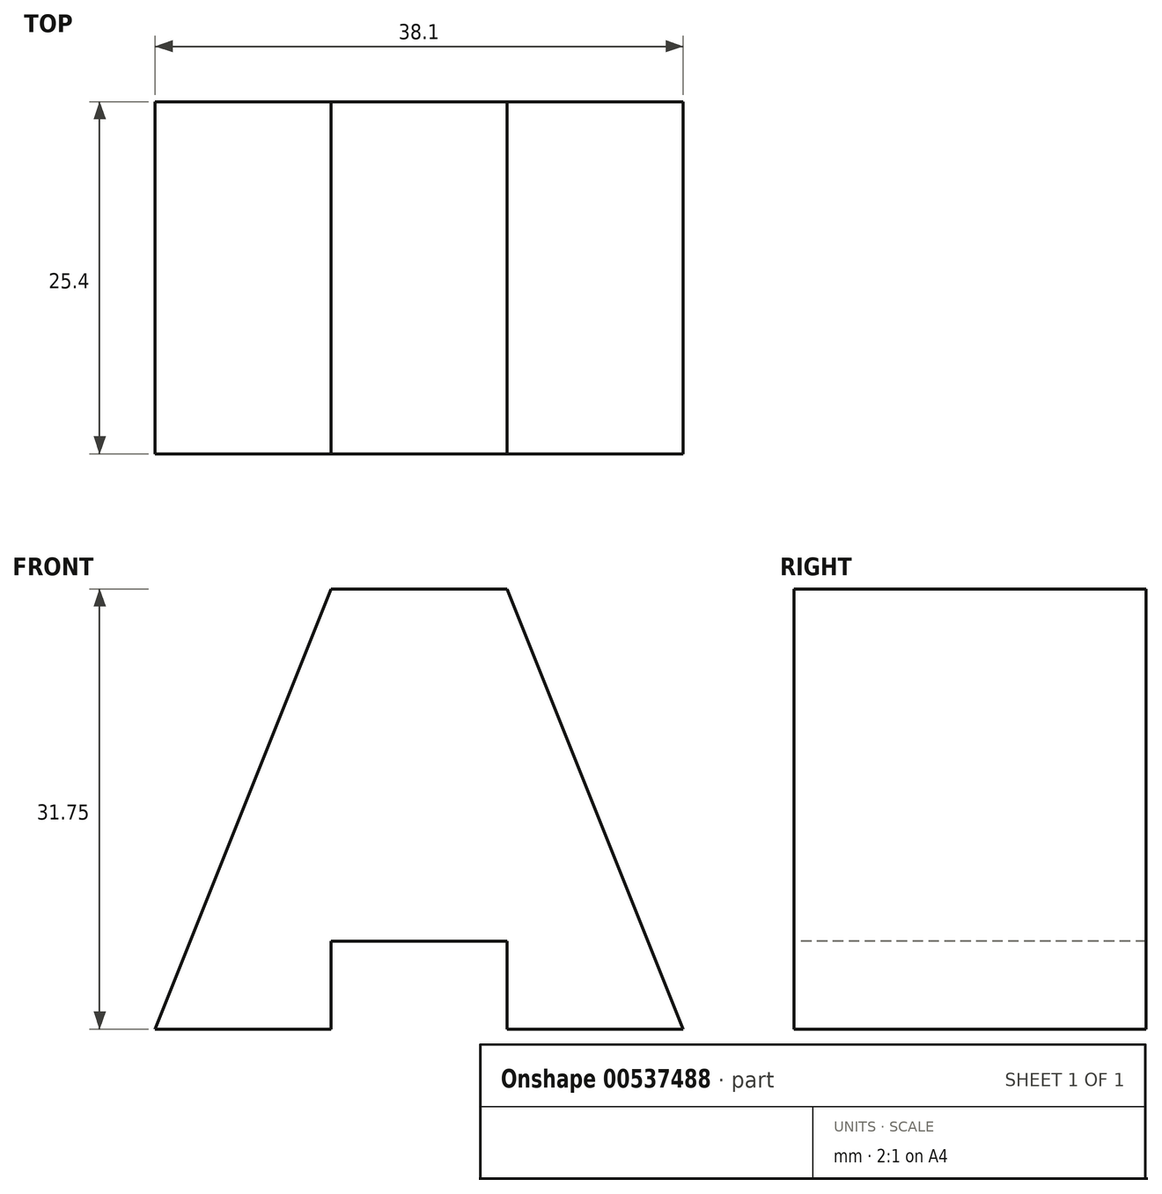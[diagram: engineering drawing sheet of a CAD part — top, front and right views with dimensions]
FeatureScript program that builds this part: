
annotation { "Feature Type Name" : "Feature", "Feature Type Description" : "" }
export const myFeature = defineFeature(function(context is Context, id is Id, definition is map)
    precondition{}
    {
        {
            var Q0;
            Q0=qCreatedBy(makeId("Front.planeOp"),FACE);
            var sketch = newSketch(context, id + "F0", { "sketchPlane" : qUnion([Q0])});
            skLineSegment(sketch, "E0", {"start": v(0, 0) * mm, "end": v(38.1, 0) * mm});
            skLineSegment(sketch, "E1", {"start": v(38.1, 0) * mm, "end": v(25.4, 31.75) * mm});
            skLineSegment(sketch, "E2", {"start": v(25.4, 31.75) * mm, "end": v(12.7, 31.75) * mm});
            skLineSegment(sketch, "E3", {"start": v(12.7, 31.75) * mm, "end": v(0, 0) * mm});
            skPoint(sketch, "E4.endSnap0", {"position": v(19.05, 0) * mm});
            skSolve(sketch);
        }
        {
            var Q0;
            Q0 = qSketchRegion(id + "F0", true);
            var Q1;
            Q1 = qConstructionFilter(qBodyType(qCreatedBy(id + "F0" ,EDGE), BodyType.WIRE), ConstructionObject.NO);
            extrude(context, id + "F1", {"entities" : qUnion([Q0]), "surfaceEntities" : qUnion([Q1]), "depth" : 25.4 * mm, "offsetDistance" : 25.4 * mm});
        }
        {
            var Q0;
            Q0=makeQuery(id+"F1.opExtrude","CAP_FACE",FACE,{"disambiguationData":[OSD([sQuery(id+"F0.wireOp",EDGE,"E0"),sQuery(id+"F0.wireOp",EDGE,"E1"),sQuery(id+"F0.wireOp",EDGE,"E2"),sQuery(id+"F0.wireOp",EDGE,"E3")])],"isStart":false});
            var sketch = newSketch(context, id + "F2", { "sketchPlane" : qUnion([Q0])});
            skLineSegment(sketch, "E5", {"start": v(12.7, 0) * mm, "end": v(12.7, 6.35) * mm});
            skLineSegment(sketch, "E6", {"start": v(12.7, 6.35) * mm, "end": v(25.4, 6.35) * mm});
            skLineSegment(sketch, "E7", {"start": v(25.4, 6.35) * mm, "end": v(25.4, 0) * mm});
            skLineSegment(sketch, "E8", {"start": v(25.4, 0) * mm, "end": v(12.7, 0) * mm});
            skSolve(sketch);
        }
        {
            var Q0;
            Q0 = qSketchRegion(id + "F2", true);
            extrude(context, id + "F3", {"entities" : qUnion([Q0]), "operationType" : NewBodyOperationType.REMOVE, "oppositeDirection" : true, "depth" : 25.4 * mm, "offsetDistance" : 25.4 * mm});
        }
    });
